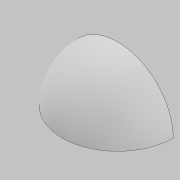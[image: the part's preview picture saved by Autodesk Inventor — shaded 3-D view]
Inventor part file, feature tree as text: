
AUTODESK INVENTOR PART (.ipt)
format: ipt  version: 2021 (Build 250183000, 183)  size: 118,272 bytes
history: native  units: mm
features: other x2, revolve x1, sketch x1
ambient origin geometry x8: Origin, YZ Plane, XZ Plane, XY Plane, X Axis, Y Axis, Z Axis, Center Point
bodies: Body1 (feature_tree)
feature tree (4):
  revolve  "Revolution1"  [1 undecoded]
  other  "tangent1"
  other  "tangent2"
  sketch  "Sketch1"  dims[d0=10.0mm d1=890.0mm d2=0.0mm d3=0.0mm d6=180.0deg d7=900.0mm d8=-900.0mm]
note: 1 required parameter value undecoded (feature->parameter linkage not recoverable at this tier; creation-order binding heuristic only, values carry confidence <= 0.55)
